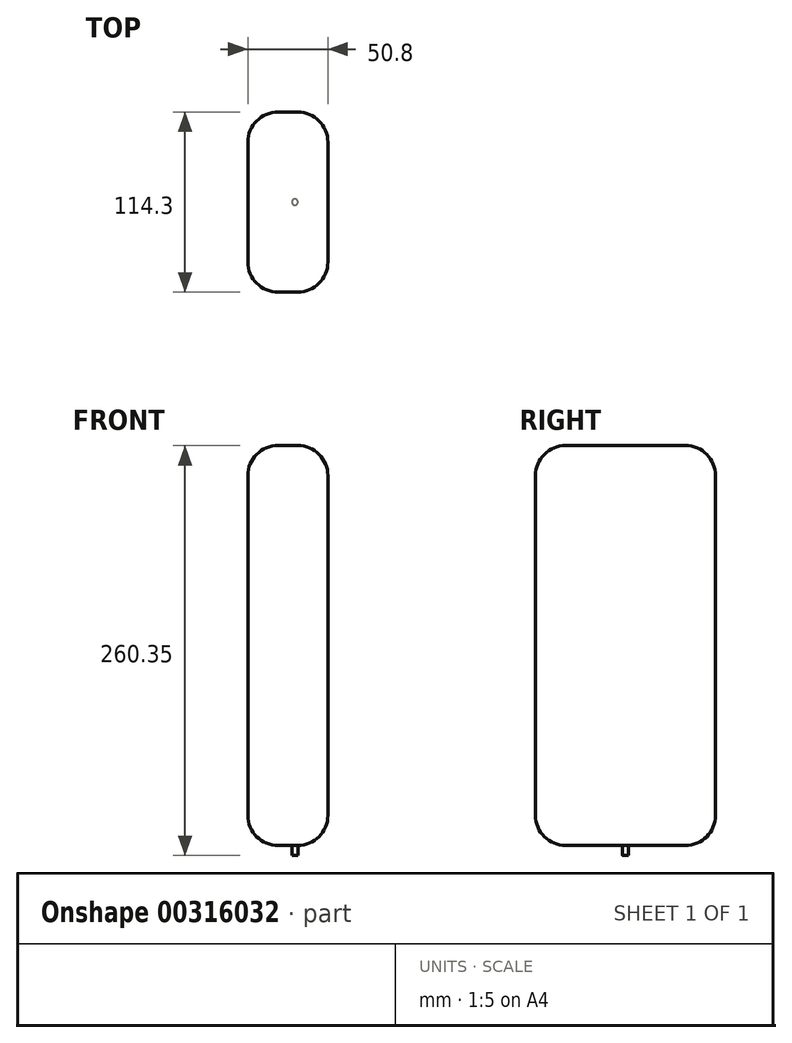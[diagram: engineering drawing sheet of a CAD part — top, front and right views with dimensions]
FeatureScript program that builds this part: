
annotation { "Feature Type Name" : "Feature", "Feature Type Description" : "" }
export const myFeature = defineFeature(function(context is Context, id is Id, definition is map)
    precondition{}
    {
        {
            var Q0;
            Q0=qCreatedBy(makeId("Top.planeOp"),FACE);
            var sketch = newSketch(context, id + "F0", { "sketchPlane" : qUnion([Q0])});
            skLineSegment(sketch, "E0.bottom", {"start": v(25.4, 57.15) * mm, "end": v(-25.4, 57.15) * mm});
            skLineSegment(sketch, "E0.top", {"start": v(25.4, -57.15) * mm, "end": v(-25.4, -57.15) * mm});
            skLineSegment(sketch, "E0.left", {"start": v(25.4, 57.15) * mm, "end": v(25.4, -57.15) * mm});
            skLineSegment(sketch, "E0.right", {"start": v(-25.4, 57.15) * mm, "end": v(-25.4, -57.15) * mm});
            skPoint(sketch, "E0.middle", {"position": v(0, 0) * mm});
            skSolve(sketch);
        }
        {
            var Q0;
            Q0=makeQuery(id+"F0.imprint","IMPRINT",FACE,{"disambiguationData":[TD([[makeQuery(id+"F0.imprint","IMPRINT",EDGE,{"derivedFrom":sQuery(id+"F0.wireOp",EDGE,"E0.bottom")}),1.0]])]});
            extrude(context, id + "F1", {"entities" : qUnion([Q0]), "depth" : 254 * mm});
        }
        {
            var Q0;
            Q0=makeQuery(id+"F1.opExtrude","CAP_FACE",FACE,{"disambiguationData":[OSD([sQuery(id+"F0.wireOp",EDGE,"E0.bottom"),sQuery(id+"F0.wireOp",EDGE,"E0.top"),sQuery(id+"F0.wireOp",EDGE,"E0.left"),sQuery(id+"F0.wireOp",EDGE,"E0.right")])],"isStart":true});
            var sketch = newSketch(context, id + "F2", { "sketchPlane" : qUnion([Q0])});
            skCircle(sketch, "E1", {"center": v(4.44, 0) * mm, "radius": 1.9 * mm});
            skSolve(sketch);
        }
        {
            var Q0;
            Q0 = qSketchRegion(id + "F2", true);
            extrude(context, id + "F3", {"entities" : qUnion([Q0]), "operationType" : NewBodyOperationType.ADD, "depth" : 6.35 * mm});
        }
        {
            var Q0;
            Q0=makeQuery(id+"F1.opExtrude","SWEPT_FACE",FACE,{"disambiguationData":[OSD([sQuery(id+"F0.wireOp",EDGE,"E0.right")])]});
            var Q1;
            Q1=makeQuery(id+"F1.opExtrude","SWEPT_FACE",FACE,{"disambiguationData":[OSD([sQuery(id+"F0.wireOp",EDGE,"E0.top")])]});
            var Q2;
            Q2=makeQuery(id+"F1.opExtrude","CAP_FACE",FACE,{"disambiguationData":[OSD([sQuery(id+"F0.wireOp",EDGE,"E0.bottom"),sQuery(id+"F0.wireOp",EDGE,"E0.top"),sQuery(id+"F0.wireOp",EDGE,"E0.left"),sQuery(id+"F0.wireOp",EDGE,"E0.right")])],"isStart":false});
            var Q3;
            Q3=makeQuery(id+"F1.opExtrude","SWEPT_FACE",FACE,{"disambiguationData":[OSD([sQuery(id+"F0.wireOp",EDGE,"E0.bottom")])]});
            var Q4;
            Q4=makeQuery(id+"F1.opExtrude","CAP_EDGE",EDGE,{"disambiguationData":[OSD([sQuery(id+"F0.wireOp",EDGE,"E0.left")])],"isStart":true});
            fillet(context, id + "F4", {"entities" : qUnion([Q0, Q1, Q2, Q3, Q4]), "radius" : 19.05 * mm, "tangentPropagation" : true, "allowEdgeOverflow" : false});
        }
    });
